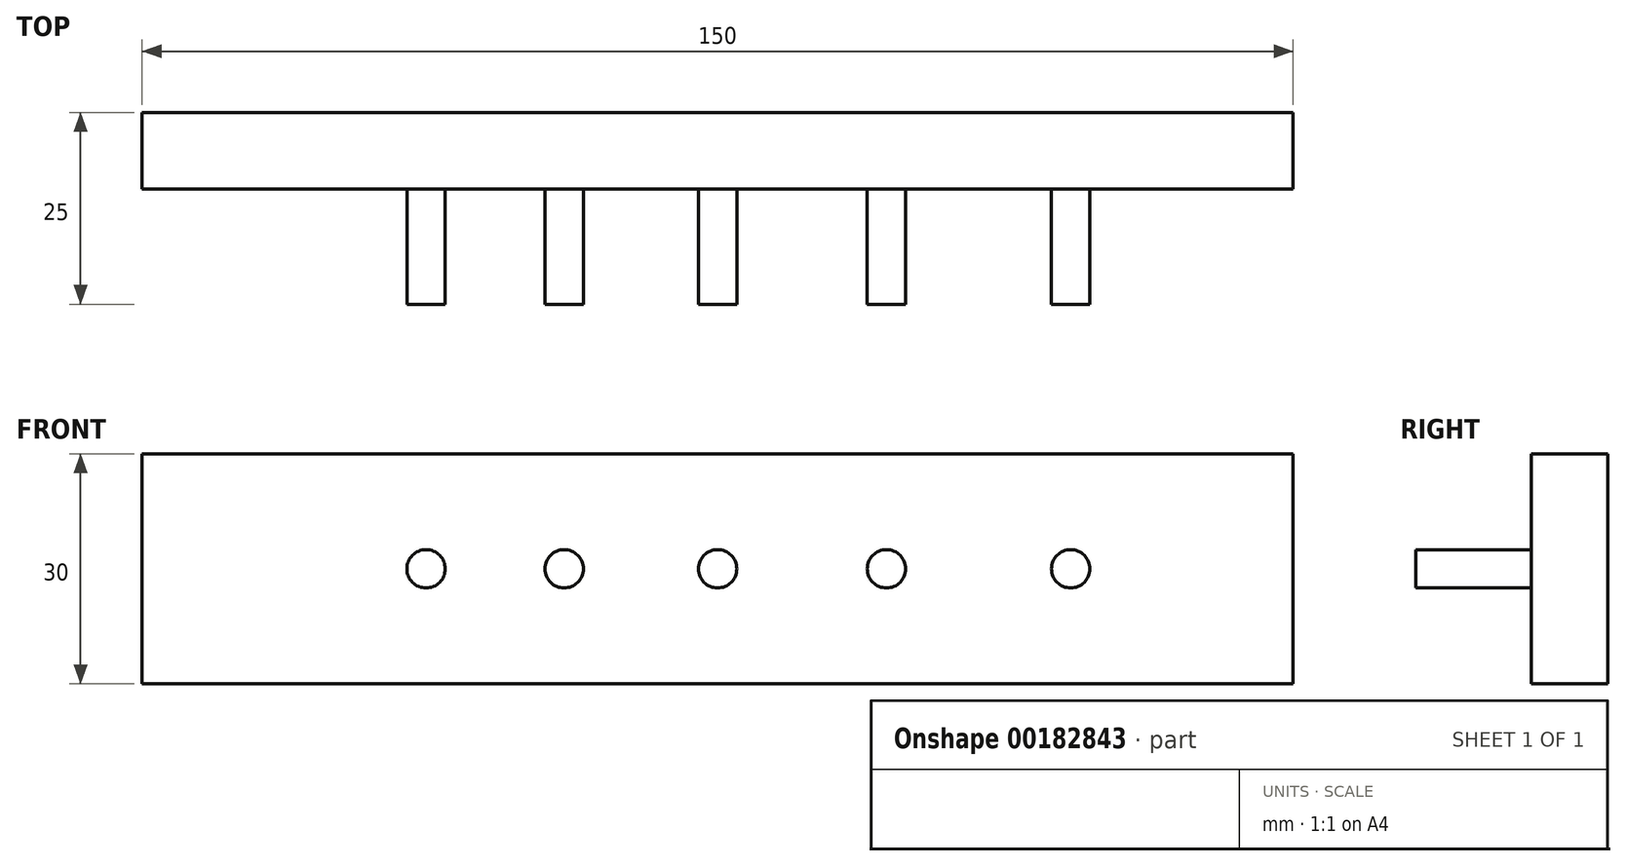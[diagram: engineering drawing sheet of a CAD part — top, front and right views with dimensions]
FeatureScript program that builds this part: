
annotation { "Feature Type Name" : "Feature", "Feature Type Description" : "" }
export const myFeature = defineFeature(function(context is Context, id is Id, definition is map)
    precondition{}
    {
        {
            var Q0;
            Q0=qCreatedBy(makeId("Front.planeOp"),FACE);
            var sketch = newSketch(context, id + "F0", { "sketchPlane" : qUnion([Q0])});
            skLineSegment(sketch, "E0.bottom", {"start": v(-75, 15) * mm, "end": v(75, 15) * mm});
            skLineSegment(sketch, "E0.top", {"start": v(-75, -15) * mm, "end": v(75, -15) * mm});
            skLineSegment(sketch, "E0.left", {"start": v(-75, 15) * mm, "end": v(-75, -15) * mm});
            skLineSegment(sketch, "E0.right", {"start": v(75, 15) * mm, "end": v(75, -15) * mm});
            skSolve(sketch);
        }
        {
            var Q0;
            Q0=makeQuery(id+"F0.imprint","IMPRINT",FACE,{"disambiguationData":[TD([[makeQuery(id+"F0.imprint","IMPRINT",EDGE,{"derivedFrom":sQuery(id+"F0.wireOp",EDGE,"E0.bottom")}),-1.0]])]});
            extrude(context, id + "F1", {"entities" : qUnion([Q0]), "oppositeDirection" : true, "depth" : 10 * mm});
        }
        {
            var Q0;
            Q0=makeQuery(id+"F1.opExtrude","CAP_FACE",FACE,{"disambiguationData":[OSD([sQuery(id+"F0.wireOp",EDGE,"E0.bottom"),sQuery(id+"F0.wireOp",EDGE,"E0.top"),sQuery(id+"F0.wireOp",EDGE,"E0.left"),sQuery(id+"F0.wireOp",EDGE,"E0.right")])],"isStart":true});
            var sketch = newSketch(context, id + "F2", { "sketchPlane" : qUnion([Q0])});
            skCircle(sketch, "E1", {"center": v(0, 0) * mm, "radius": 2.5 * mm});
            skCircle(sketch, "E2", {"center": v(22, 0) * mm, "radius": 2.5 * mm});
            skCircle(sketch, "E3", {"center": v(46, 0) * mm, "radius": 2.5 * mm});
            skCircle(sketch, "E4", {"center": v(-20, 0) * mm, "radius": 2.5 * mm});
            skCircle(sketch, "E5", {"center": v(-38, 0) * mm, "radius": 2.5 * mm});
            skSolve(sketch);
        }
        {
            var Q0;
            Q0=makeQuery(id+"F2.imprint","IMPRINT",FACE,{"disambiguationData":[TD([[makeQuery(id+"F2.imprint","IMPRINT",EDGE,{"derivedFrom":sQuery(id+"F2.wireOp",EDGE,"E5")}),1.0]])]});
            var Q1;
            Q1=makeQuery(id+"F2.imprint","IMPRINT",FACE,{"disambiguationData":[TD([[makeQuery(id+"F2.imprint","IMPRINT",EDGE,{"derivedFrom":sQuery(id+"F2.wireOp",EDGE,"E4")}),1.0]])]});
            var Q2;
            Q2=makeQuery(id+"F2.imprint","IMPRINT",FACE,{"disambiguationData":[TD([[makeQuery(id+"F2.imprint","IMPRINT",EDGE,{"derivedFrom":sQuery(id+"F2.wireOp",EDGE,"E1")}),1.0]])]});
            var Q3;
            Q3=makeQuery(id+"F2.imprint","IMPRINT",FACE,{"disambiguationData":[TD([[makeQuery(id+"F2.imprint","IMPRINT",EDGE,{"derivedFrom":sQuery(id+"F2.wireOp",EDGE,"E2")}),1.0]])]});
            var Q4;
            Q4=makeQuery(id+"F2.imprint","IMPRINT",FACE,{"disambiguationData":[TD([[makeQuery(id+"F2.imprint","IMPRINT",EDGE,{"derivedFrom":sQuery(id+"F2.wireOp",EDGE,"E3")}),1.0]])]});
            extrude(context, id + "F3", {"entities" : qUnion([Q0, Q1, Q2, Q3, Q4]), "operationType" : NewBodyOperationType.ADD, "depth" : 15 * mm});
        }
    });
